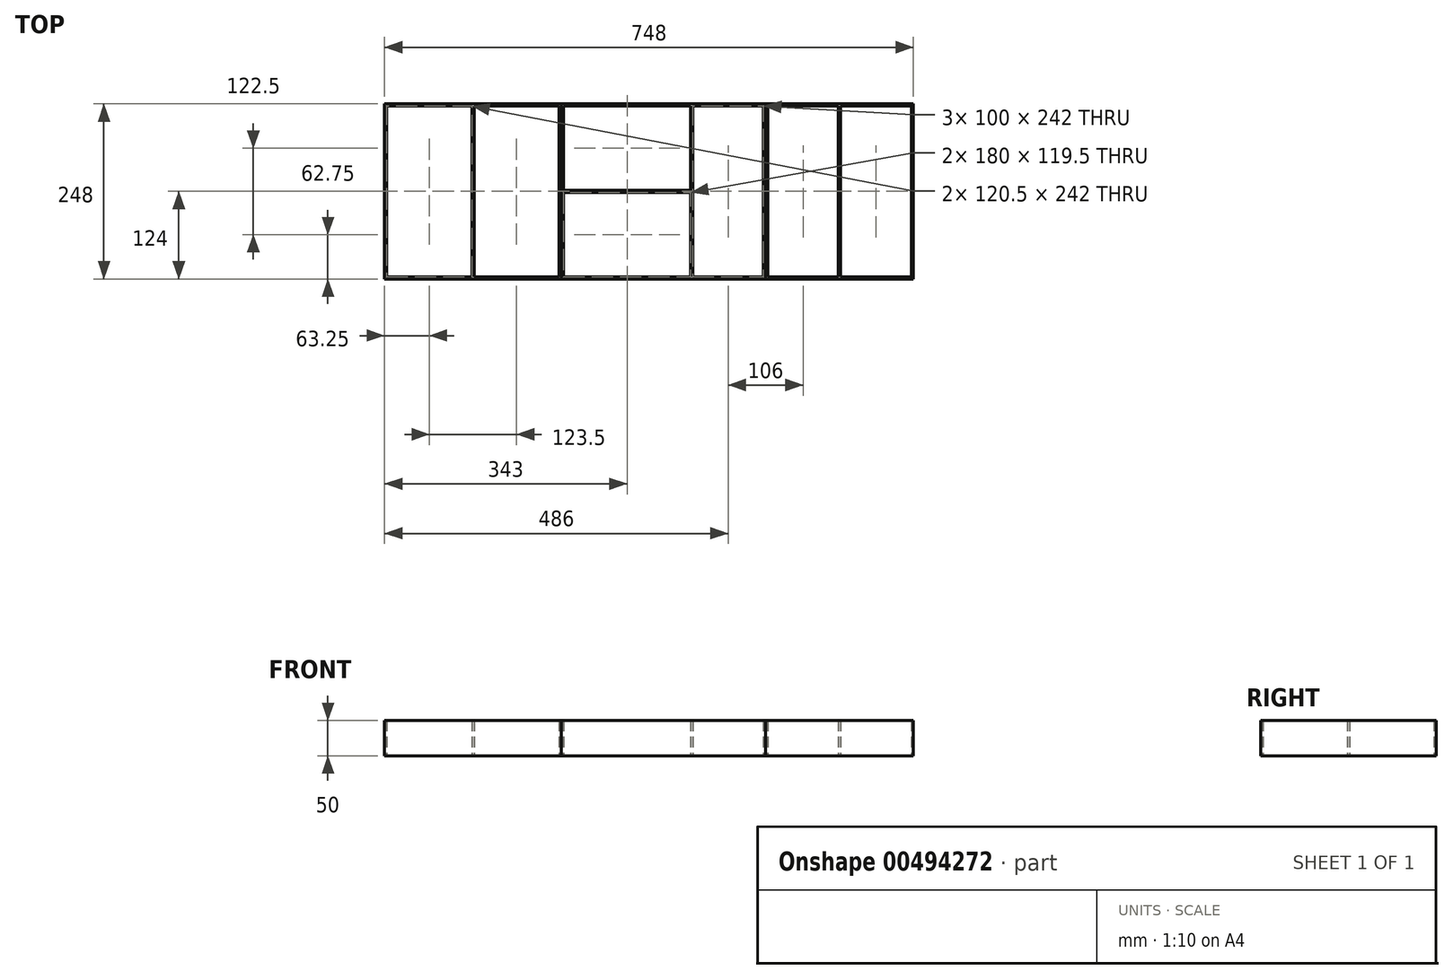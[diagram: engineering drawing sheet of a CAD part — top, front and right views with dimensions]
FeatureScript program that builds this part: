
annotation { "Feature Type Name" : "Feature", "Feature Type Description" : "" }
export const myFeature = defineFeature(function(context is Context, id is Id, definition is map)
    precondition{}
    {
        {
            var Q0;
            Q0=qCreatedBy(makeId("Top.planeOp"),FACE);
            var sketch = newSketch(context, id + "F0", { "sketchPlane" : qUnion([Q0])});
            skLineSegment(sketch, "E0.bottom", {"start": v(0, 0) * mm, "end": v(748, 0) * mm});
            skLineSegment(sketch, "E0.top", {"start": v(0, 248) * mm, "end": v(748, 248) * mm});
            skLineSegment(sketch, "E0.left", {"start": v(0, 0) * mm, "end": v(0, 248) * mm});
            skLineSegment(sketch, "E0.right", {"start": v(748, 0) * mm, "end": v(748, 248) * mm});
            skLineSegment(sketch, "E1.bottom", {"start": v(645, 245) * mm, "end": v(745, 245) * mm});
            skLineSegment(sketch, "E1.top", {"start": v(645, 3) * mm, "end": v(745, 3) * mm});
            skLineSegment(sketch, "E1.left", {"start": v(645, 245) * mm, "end": v(645, 3) * mm});
            skLineSegment(sketch, "E1.right", {"start": v(745, 245) * mm, "end": v(745, 3) * mm});
            skLineSegment(sketch, "E2.bottom", {"start": v(542, 245) * mm, "end": v(642, 245) * mm});
            skLineSegment(sketch, "E2.top", {"start": v(542, 3) * mm, "end": v(642, 3) * mm});
            skLineSegment(sketch, "E2.left", {"start": v(539, 245) * mm, "end": v(539, 3) * mm});
            skLineSegment(sketch, "E2.right", {"start": v(642, 245) * mm, "end": v(642, 3) * mm});
            skLineSegment(sketch, "E3.bottom", {"start": v(436, 245) * mm, "end": v(536, 245) * mm});
            skLineSegment(sketch, "E3.top", {"start": v(436, 3) * mm, "end": v(536, 3) * mm});
            skLineSegment(sketch, "E3.left", {"start": v(436, 245) * mm, "end": v(436, 3) * mm});
            skLineSegment(sketch, "E3.right", {"start": v(536, 245) * mm, "end": v(536, 3) * mm});
            skLineSegment(sketch, "E4.bottom", {"start": v(433, 245) * mm, "end": v(253, 245) * mm});
            skLineSegment(sketch, "E4.top", {"start": v(433, 125.5) * mm, "end": v(253, 125.5) * mm});
            skLineSegment(sketch, "E4.left", {"start": v(433, 245) * mm, "end": v(433, 125.5) * mm});
            skLineSegment(sketch, "E4.right", {"start": v(253, 245) * mm, "end": v(253, 125.5) * mm});
            skLineSegment(sketch, "E5.bottom", {"start": v(253, 122.5) * mm, "end": v(433, 122.5) * mm});
            skLineSegment(sketch, "E5.top", {"start": v(253, 3) * mm, "end": v(433, 3) * mm});
            skLineSegment(sketch, "E5.left", {"start": v(253, 122.5) * mm, "end": v(253, 3) * mm});
            skLineSegment(sketch, "E5.right", {"start": v(433, 122.5) * mm, "end": v(433, 3) * mm});
            skLineSegment(sketch, "E6.bottom", {"start": v(247, 245) * mm, "end": v(126.5, 245) * mm});
            skLineSegment(sketch, "E6.top", {"start": v(247, 3) * mm, "end": v(126.5, 3) * mm});
            skLineSegment(sketch, "E6.left", {"start": v(250, 245) * mm, "end": v(250, 3) * mm});
            skLineSegment(sketch, "E6.right", {"start": v(126.5, 245) * mm, "end": v(126.5, 3) * mm});
            skLineSegment(sketch, "E7.bottom", {"start": v(123.5, 245) * mm, "end": v(3, 245) * mm});
            skLineSegment(sketch, "E7.top", {"start": v(123.5, 3) * mm, "end": v(3, 3) * mm});
            skLineSegment(sketch, "E7.left", {"start": v(123.5, 245) * mm, "end": v(123.5, 3) * mm});
            skLineSegment(sketch, "E7.right", {"start": v(3, 245) * mm, "end": v(3, 3) * mm});
            skLineSegment(sketch, "E8", {"start": v(123.5, 245) * mm, "end": v(126.5, 245) * mm, "construction": true});
            skLineSegment(sketch, "E9", {"start": v(250, 245) * mm, "end": v(253, 245) * mm, "construction": true});
            skLineSegment(sketch, "E10", {"start": v(433, 245) * mm, "end": v(436, 245) * mm, "construction": true});
            skLineSegment(sketch, "E11", {"start": v(536, 245) * mm, "end": v(539, 245) * mm, "construction": true});
            skLineSegment(sketch, "E12", {"start": v(642, 245) * mm, "end": v(645, 245) * mm, "construction": true});
            skLineSegment(sketch, "E13", {"start": v(745, 245) * mm, "end": v(748, 245) * mm, "construction": true});
            skLineSegment(sketch, "E14", {"start": v(745, 245) * mm, "end": v(745, 248) * mm, "construction": true});
            skLineSegment(sketch, "E15", {"start": v(3, 245) * mm, "end": v(0, 245) * mm, "construction": true});
            skLineSegment(sketch, "E16", {"start": v(745, 3) * mm, "end": v(745, 0) * mm, "construction": true});
            skLineSegment(sketch, "E17", {"start": v(253, 125.5) * mm, "end": v(253, 122.5) * mm, "construction": true});
            skLineSegment(sketch, "E18", {"start": v(539, 245) * mm, "end": v(539, 248) * mm});
            skLineSegment(sketch, "E19", {"start": v(539, 3) * mm, "end": v(539, 0) * mm});
            skLineSegment(sketch, "E20", {"start": v(250, 245) * mm, "end": v(250, 248) * mm});
            skLineSegment(sketch, "E21", {"start": v(250, 3) * mm, "end": v(250, 0) * mm});
            skLineSegment(sketch, "E22", {"start": v(542, 245) * mm, "end": v(542, 3) * mm});
            skLineSegment(sketch, "E23", {"start": v(247, 3) * mm, "end": v(247, 245) * mm});
            skLineSegment(sketch, "E24", {"start": v(542, 245) * mm, "end": v(539, 245) * mm, "construction": true});
            skLineSegment(sketch, "E25", {"start": v(247, 245) * mm, "end": v(250, 245) * mm, "construction": true});
            skSolve(sketch);
        }
        {
            var Q0;
            {var subQ1=sQuery(id+"F0.wireOp",EDGE,"E0.right");Q0=makeQuery(id+"F0.imprint","IMPRINT",FACE,{"disambiguationData":[TD([[makeQuery(id+"F0.imprint","IMPRINT",EDGE,{"derivedFrom":subQ1}),1.0]])]});}
            extrude(context, id + "F1", {"entities" : qUnion([Q0]), "depth" : 50 * mm});
        }
        {
            var Q0;
            Q0=makeQuery(id+"F0.imprint","IMPRINT",FACE,{"disambiguationData":[TD([[makeQuery(id+"F0.imprint","IMPRINT",EDGE,{"derivedFrom":sQuery(id+"F0.wireOp",EDGE,"E2.left")}),-1.0]])]});
            extrude(context, id + "F2", {"entities" : qUnion([Q0]), "depth" : 50 * mm});
        }
        {
            var Q0;
            {var subQ0=sQuery(id+"F0.wireOp",EDGE,"E0.left");Q0=makeQuery(id+"F0.imprint","IMPRINT",FACE,{"disambiguationData":[TD([[makeQuery(id+"F0.imprint","IMPRINT",EDGE,{"derivedFrom":subQ0}),-1.0]])]});}
            extrude(context, id + "F3", {"entities" : qUnion([Q0]), "depth" : 50 * mm});
        }
    });
